# Revit family: Shower_Head-GROHE-Rainshower_Cosmopolitan_160-27135_Series
name_source: partatom
category: Plumbing Fixtures
revit_build: Autodesk Revit 2014 (Build: 20130308_1515(x64)
units: mm (PartAtom-declared; Revit-internal decimal feet)

## types (3) — shared parameters
Assembly Code = D2010700
CW Connection = Yes
CWFU = 3
Cold Water Connection Diameter = 1/2"
Cold Water Connection Radius = 1/4"
Default Elevation = 0"
Description = Rainshower® Cosmopolitan 160
Flow Rate = 2.0GPM (7.6L/min)
HW Connection = Yes
HWFU = 3
Height = 4"
Hot Water Connection Diameter = 1"
Hot Water Connection Radius = 1/4"
Manufacturer = GROHE
Price = Prices may vary. Please consult Manufacturer Representative for most up-to-date price list.
Product Page URL = https://www.grohe.com
Tempered Water Connection Diameter = 1/2"
Tempered Water Connection Radius = 1/4"
URL = http://www.grohe.com
Vent Connection = No
WFU = 4
Warranty Documentation Link = https://cdn.cloud.grohe.com
Waste Connection = No
Width = 6 5/16"
cUPC Compliant = Yes

## per-type parameters (varying)
| type | Finish | Material | Type Comments |
| 27135000 | Metal-Grohe-000-Chrome | Metal-Grohe-000-Chrome |  |
| 27135ZB0 | Metal-Grohe-ZB0-Oil Rubbed Bronze | Metal-Grohe-ZB0-Oil Rubbed Bronze | *DISCONTINUED* |
| 27135EN0 | Metal-Grohe-EN0-Brushed Nickel | Metal-Grohe-EN0-Brushed Nickel |  |

note: column(s) folded — value = type name in every type: Model

## geometry (parser evidence)
native form markers: Sweep x1
no freeform markers — native parametric forms only
